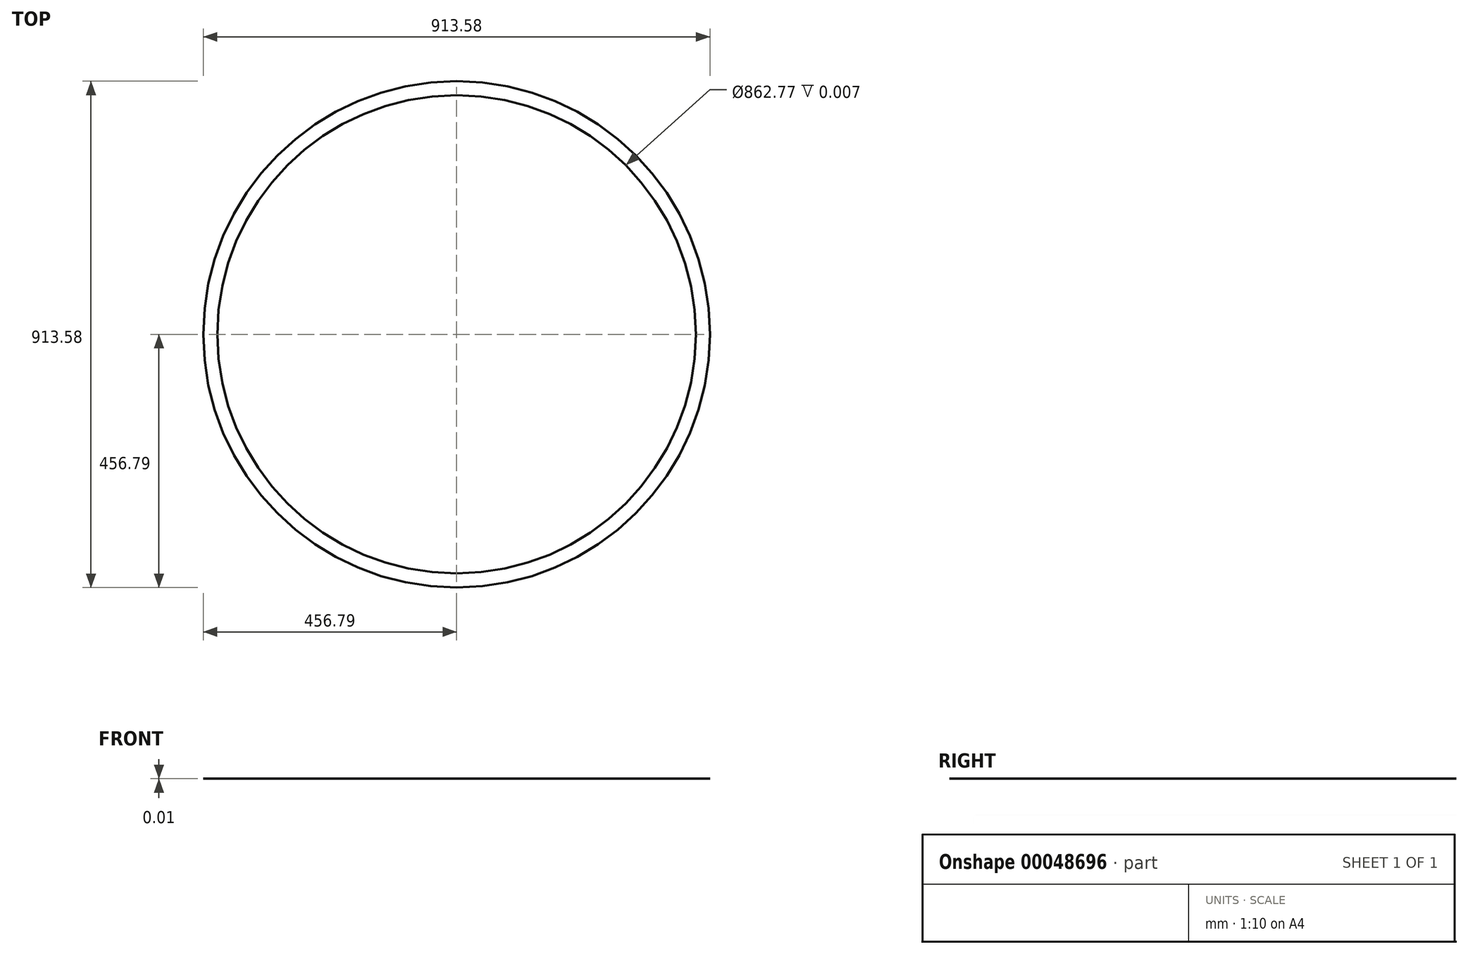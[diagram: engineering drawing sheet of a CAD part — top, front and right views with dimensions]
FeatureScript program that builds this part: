
annotation { "Feature Type Name" : "Feature", "Feature Type Description" : "" }
export const myFeature = defineFeature(function(context is Context, id is Id, definition is map)
    precondition{}
    {
        {
            var Q0;
            Q0=qCreatedBy(makeId("Top.planeOp"),FACE);
            var sketch = newSketch(context, id + "F0", { "sketchPlane" : qUnion([Q0])});
            skCircle(sketch, "E0", {"center": v(0, 0) * mm, "radius": 456.79 * mm});
            skCircle(sketch, "E1", {"center": v(0, 0) * mm, "radius": 431.39 * mm});
            skSolve(sketch);
        }
        {
            var Q0;
            Q0 = qSketchRegion(id + "F0", true);
            extrude(context, id + "F1", {"entities" : qUnion([Q0]), "depth" : 3 / 457.2 * mm});
        }
    });
